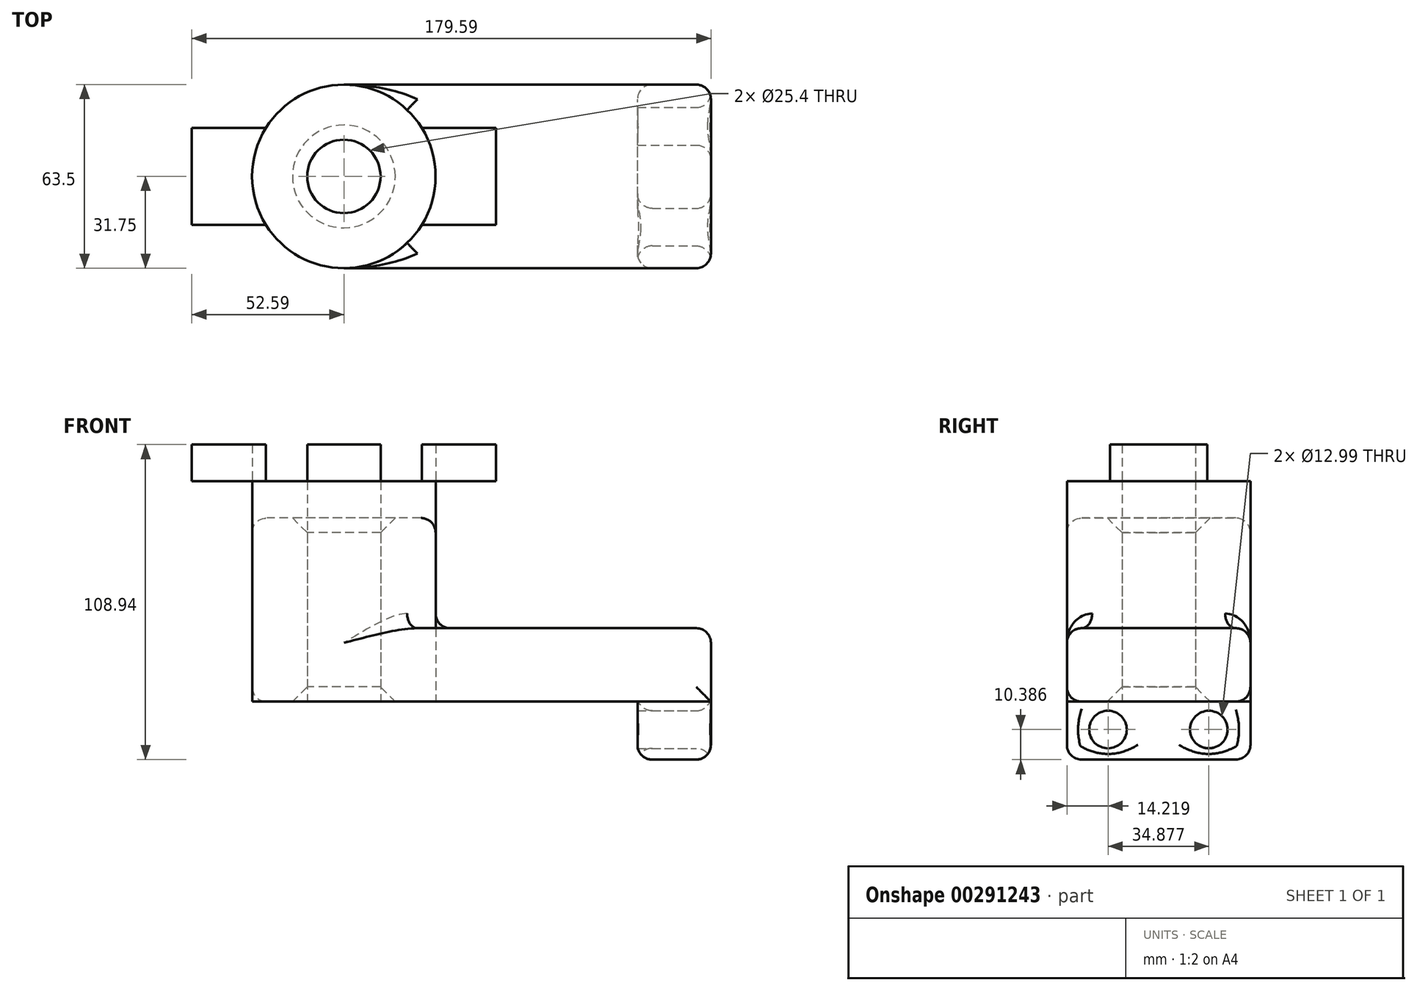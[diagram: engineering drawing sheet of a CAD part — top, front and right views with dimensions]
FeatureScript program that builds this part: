
annotation { "Feature Type Name" : "Feature", "Feature Type Description" : "" }
export const myFeature = defineFeature(function(context is Context, id is Id, definition is map)
    precondition{}
    {
        {
            var Q0;
            Q0=qCreatedBy(makeId("Top.planeOp"),FACE);
            var sketch = newSketch(context, id + "F0", { "sketchPlane" : qUnion([Q0])});
            skLineSegment(sketch, "E0.bottom", {"start": v(0, 0) * mm, "end": v(127, 0) * mm});
            skLineSegment(sketch, "E0.top", {"start": v(0, 63.5) * mm, "end": v(127, 63.5) * mm});
            skLineSegment(sketch, "E0.left", {"start": v(0, 0) * mm, "end": v(0, 63.5) * mm});
            skLineSegment(sketch, "E0.right", {"start": v(127, 0) * mm, "end": v(127, 63.5) * mm});
            skCircle(sketch, "E1", {"center": v(0, 31.75) * mm, "radius": 31.75 * mm});
            skCircle(sketch, "E2", {"center": v(0, 31.75) * mm, "radius": 12.7 * mm});
            skSolve(sketch);
        }
        {
            var Q0;
            Q0 = qSketchRegion(id + "F0", true);
            extrude(context, id + "F1", {"entities" : qUnion([Q0]), "depth" : 25.4 * mm});
        }
        {
            var Q0;
            {var subQ1=sQuery(id+"F0.wireOp",EDGE,"E0.left");var subQ3=sQuery(id+"F0.wireOp",EDGE,"E2");var subQ4=makeQuery(id+"F0.imprint","INTERSECT",VERTEX,{"disambiguationData":[OD(0.0)],"derivedFrom":[subQ1,subQ3]});Q0=makeQuery(id+"F0.imprint","IMPRINT",FACE,{"disambiguationData":[TD([[makeQuery(id+"F0.imprint","IMPRINT",EDGE,{"disambiguationData":[TD([[subQ4,1.0]])],"derivedFrom":subQ3}),-1.0]])]});}
            var Q1;
            {var subQ1=sQuery(id+"F0.wireOp",EDGE,"E0.left");var subQ3=sQuery(id+"F0.wireOp",EDGE,"E2");var subQ4=makeQuery(id+"F0.imprint","INTERSECT",VERTEX,{"disambiguationData":[OD(0.0)],"derivedFrom":[subQ1,subQ3]});Q1=makeQuery(id+"F0.imprint","IMPRINT",FACE,{"disambiguationData":[TD([[makeQuery(id+"F0.imprint","IMPRINT",EDGE,{"disambiguationData":[TD([[subQ4,-1.0]])],"derivedFrom":subQ3}),-1.0]])]});}
            extrude(context, id + "F2", {"entities" : qUnion([Q0, Q1]), "operationType" : NewBodyOperationType.ADD, "depth" : 63.5 * mm});
        }
        {
            var Q0;
            Q0=makeQuery(id+"F1.opExtrude","SWEPT_FACE",FACE,{"disambiguationData":[OSD([sQuery(id+"F0.wireOp",EDGE,"E0.right")])]});
            var sketch = newSketch(context, id + "F3", { "sketchPlane" : qUnion([Q0])});
            skLineSegment(sketch, "E3.bottom", {"start": v(0, 25.4) * mm, "end": v(63.5, 25.4) * mm});
            skLineSegment(sketch, "E3.top", {"start": v(0, -20.04) * mm, "end": v(63.5, -20.04) * mm});
            skLineSegment(sketch, "E3.left", {"start": v(0, 25.4) * mm, "end": v(0, -20.04) * mm});
            skLineSegment(sketch, "E3.right", {"start": v(63.5, 25.4) * mm, "end": v(63.5, -20.04) * mm});
            skSolve(sketch);
        }
        {
            var Q0;
            {var subQ0=sQuery(id+"F3.wireOp",EDGE,"E3.top");Q0=makeQuery(id+"F3.imprint","IMPRINT",FACE,{"disambiguationData":[TD([[makeQuery(id+"F3.imprint","IMPRINT",EDGE,{"derivedFrom":subQ0}),1.0]])]});}
            var sketch = newSketch(context, id + "F4", { "sketchPlane" : qUnion([Q0])});
            skLineSegment(sketch, "E4", {"start": v(31.66, 0) * mm, "end": v(31.66, -20.41) * mm, "construction": true});
            skPoint(sketch, "E5.centerSnap0", {"position": v(31.66, -10.2) * mm});
            skCircle(sketch, "E6", {"center": v(14.22, -9.65) * mm, "radius": 6.5 * mm});
            skCircle(sketch, "E7.MirrorC", {"center": v(49.1, -9.65) * mm, "radius": 6.5 * mm});
            skSolve(sketch);
        }
        {
            var Q0;
            Q0=makeQuery(id+"F4.imprint","IMPRINT",FACE,{"disambiguationData":[TD([[makeQuery(id+"F4.imprint","IMPRINT",EDGE,{"derivedFrom":sQuery(id+"F4.wireOp",EDGE,"E6")}),-1.0]])]});
            extrude(context, id + "F5", {"entities" : qUnion([Q0]), "oppositeDirection" : true, "depth" : 25.4 * mm});
        }
        {
            var Q0;
            Q0=makeQuery(id+"F1.opExtrude","CAP_EDGE",EDGE,{"disambiguationData":[OSD([sQuery(id+"F0.wireOp",EDGE,"E0.bottom")])],"isStart":false});
            var Q1;
            {var subQ0=sQuery(id+"F0.wireOp",EDGE,"E1");Q1=makeQuery(id+"F2.boolean.opBoolean","INTERSECT",EDGE,{"derivedFrom":[makeQuery(id+"F1.opExtrude","CAP_FACE",FACE,{"disambiguationData":[OSD([sQuery(id+"F0.wireOp",EDGE,"E0.bottom"),sQuery(id+"F0.wireOp",EDGE,"E0.top"),sQuery(id+"F0.wireOp",EDGE,"E0.right"),subQ0,sQuery(id+"F0.wireOp",EDGE,"E2")])],"isStart":false}),makeQuery(id+"F2.opExtrude","SWEPT_FACE",FACE,{"disambiguationData":[OSD([subQ0])]})]});}
            var Q2;
            Q2=makeQuery(id+"F1.opExtrude","CAP_EDGE",EDGE,{"disambiguationData":[OSD([sQuery(id+"F0.wireOp",EDGE,"E0.top")])],"isStart":false});
            var Q3;
            Q3=makeQuery(id+"F1.opExtrude","CAP_EDGE",EDGE,{"disambiguationData":[OSD([sQuery(id+"F0.wireOp",EDGE,"E0.right")])],"isStart":false});
            var Q4;
            Q4=makeQuery(id+"F2.opExtrude","CAP_EDGE",EDGE,{"disambiguationData":[OSD([sQuery(id+"F0.wireOp",EDGE,"E1")])],"isStart":false});
            var Q5;
            Q5=makeQuery(id+"F1.opExtrude","CAP_EDGE",EDGE,{"disambiguationData":[OSD([sQuery(id+"F0.wireOp",EDGE,"E1")])],"isStart":true});
            var Q6;
            Q6=makeQuery(id+"F1.opExtrude","CAP_EDGE",EDGE,{"disambiguationData":[OSD([sQuery(id+"F0.wireOp",EDGE,"E0.bottom")])],"isStart":true});
            var Q7;
            Q7=makeQuery(id+"F1.opExtrude","CAP_EDGE",EDGE,{"disambiguationData":[OSD([sQuery(id+"F0.wireOp",EDGE,"E0.top")])],"isStart":true});
            var Q8;
            Q8=makeQuery(id+"F5.opExtrude","CAP_EDGE",EDGE,{"disambiguationData":[OSD([sQuery(id+"F3.wireOp",EDGE,"E3.right")])],"isStart":false});
            var Q9;
            Q9=makeQuery(id+"F5.opExtrude","SWEPT_EDGE",EDGE,{"disambiguationData":[OSD([sQuery(id+"F3.wireOp",EDGE,"E3.top"),sQuery(id+"F3.wireOp",EDGE,"E3.right")])]});
            var Q10;
            Q10=makeQuery(id+"F5.opExtrude","CAP_EDGE",EDGE,{"disambiguationData":[OSD([sQuery(id+"F3.wireOp",EDGE,"E3.top")])],"isStart":false});
            var Q11;
            Q11=makeQuery(id+"F5.opExtrude","CAP_EDGE",EDGE,{"disambiguationData":[OSD([sQuery(id+"F3.wireOp",EDGE,"E3.left")])],"isStart":false});
            var Q12;
            Q12=makeQuery(id+"F5.opExtrude","CAP_EDGE",EDGE,{"disambiguationData":[OSD([sQuery(id+"F3.wireOp",EDGE,"E3.top")])],"isStart":true});
            var Q13;
            Q13=makeQuery(id+"F5.opExtrude","CAP_EDGE",EDGE,{"disambiguationData":[OSD([sQuery(id+"F3.wireOp",EDGE,"E3.left")])],"isStart":true});
            var Q14;
            Q14=makeQuery(id+"F5.opExtrude","CAP_EDGE",EDGE,{"disambiguationData":[OSD([sQuery(id+"F3.wireOp",EDGE,"E3.right")])],"isStart":true});
            var Q15;
            Q15=makeQuery(id+"F5.opExtrude","CAP_EDGE",EDGE,{"disambiguationData":[OSD([sQuery(id+"F4.wireOp",EDGE,"E6")])],"isStart":true});
            var Q16;
            Q16=makeQuery(id+"F5.opExtrude","CAP_EDGE",EDGE,{"disambiguationData":[OSD([sQuery(id+"F4.wireOp",EDGE,"E6")])],"isStart":false});
            var Q17;
            Q17=makeQuery(id+"F5.opExtrude","CAP_EDGE",EDGE,{"disambiguationData":[OSD([sQuery(id+"F4.wireOp",EDGE,"E7.MirrorC")])],"isStart":true});
            var Q18;
            Q18=makeQuery(id+"F5.opExtrude","SWEPT_EDGE",EDGE,{"disambiguationData":[OSD([sQuery(id+"F3.wireOp",EDGE,"E3.top"),sQuery(id+"F3.wireOp",EDGE,"E3.left")])]});
            var Q19;
            Q19=makeQuery(id+"F1.opExtrude","SWEPT_EDGE",EDGE,{"disambiguationData":[OSD([sQuery(id+"F0.wireOp",EDGE,"E0.top"),sQuery(id+"F0.wireOp",EDGE,"E0.right")])]});
            var Q20;
            Q20=makeQuery(id+"F1.opExtrude","SWEPT_EDGE",EDGE,{"disambiguationData":[OSD([sQuery(id+"F0.wireOp",EDGE,"E0.bottom"),sQuery(id+"F0.wireOp",EDGE,"E0.right")])]});
            fillet(context, id + "F6", {"entities" : qUnion([Q0, Q1, Q2, Q3, Q4, Q5, Q6, Q7, Q8, Q9, Q10, Q11, Q12, Q13, Q14, Q15, Q16, Q17, Q18, Q19, Q20]), "radius" : 5.08 * mm, "tangentPropagation" : true, "allowEdgeOverflow" : false});
        }
        {
            var Q0;
            {var subQ0=sQuery(id+"F0.wireOp",EDGE,"E2");Q0=makeQuery(id+"F2.boolean.opBoolean","MERGE",FACE,{"derivedFrom":[makeQuery(id+"F1.opExtrude","SWEPT_FACE",FACE,{"disambiguationData":[OSD([subQ0])]}),makeQuery(id+"F2.opExtrude","SWEPT_FACE",FACE,{"disambiguationData":[OSD([subQ0])]})]});}
            chamfer(context, id + "F7", {"entities" : qUnion([Q0]), "width" : 5.08 * mm, "tangentPropagation" : true});
        }
        {
            var Q0;
            {var subQ0=sQuery(id+"F0.wireOp",EDGE,"E2");var subQ1=sQuery(id+"F0.wireOp",EDGE,"E0.left");var subQ2=makeQuery(id+"F0.imprint","INTERSECT",VERTEX,{"disambiguationData":[OD(0.0)],"derivedFrom":[subQ1,subQ0]});Q0=makeQuery(id+"F0.imprint","IMPRINT",FACE,{"disambiguationData":[TD([[makeQuery(id+"F0.imprint","IMPRINT",EDGE,{"disambiguationData":[TD([[subQ2,-1.0]])],"derivedFrom":subQ1}),1.0]])]});}
            var Q1;
            {var subQ0=sQuery(id+"F0.wireOp",EDGE,"E2");var subQ1=sQuery(id+"F0.wireOp",EDGE,"E0.left");var subQ2=makeQuery(id+"F0.imprint","INTERSECT",VERTEX,{"disambiguationData":[OD(0.0)],"derivedFrom":[subQ1,subQ0]});Q1=makeQuery(id+"F0.imprint","IMPRINT",FACE,{"disambiguationData":[TD([[makeQuery(id+"F0.imprint","IMPRINT",EDGE,{"disambiguationData":[TD([[subQ2,-1.0]])],"derivedFrom":subQ1}),-1.0]])]});}
            extrude(context, id + "F8", {"entities" : qUnion([Q0, Q1]), "depth" : 76.2 * mm});
        }
        {
            var Q0;
            Q0=makeQuery(id+"F8.opExtrude","CAP_FACE",FACE,{"disambiguationData":[OSD([sQuery(id+"F0.wireOp",EDGE,"E2")])],"isStart":false});
            var sketch = newSketch(context, id + "F9", { "sketchPlane" : qUnion([Q0])});
            skLineSegment(sketch, "E8.bottom", {"start": v(52.59, 48.53) * mm, "end": v(-52.59, 48.53) * mm});
            skLineSegment(sketch, "E8.top", {"start": v(52.59, 14.97) * mm, "end": v(-52.59, 14.97) * mm});
            skLineSegment(sketch, "E8.left", {"start": v(52.59, 48.53) * mm, "end": v(52.59, 14.97) * mm});
            skLineSegment(sketch, "E8.right", {"start": v(-52.59, 48.53) * mm, "end": v(-52.59, 14.97) * mm});
            skPoint(sketch, "E8.middle", {"position": v(0, 31.75) * mm});
            skSolve(sketch);
        }
        {
            var Q0;
            Q0=makeQuery(id+"F9.imprint","IMPRINT",FACE,{"disambiguationData":[TD([[makeQuery(id+"F9.imprint","IMPRINT",EDGE,{"derivedFrom":sQuery(id+"F9.wireOp",EDGE,"E8.bottom")}),1.0]])]});
            var Q1;
            Q1=makeQuery(id+"F9.imprint","IMPRINT",FACE,{"disambiguationData":[TD([[makeQuery(id+"F9.imprint","IMPRINT",EDGE,{"derivedFrom":makeQuery(id+"F8.opExtrude","CAP_EDGE",EDGE,{"disambiguationData":[OSD([sQuery(id+"F0.wireOp",EDGE,"E2")])],"isStart":false})}),1.0]])]});
            extrude(context, id + "F10", {"entities" : qUnion([Q0, Q1]), "operationType" : NewBodyOperationType.ADD, "depth" : 12.7 * mm});
        }
    });
